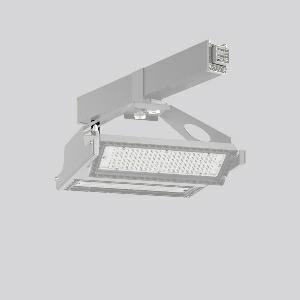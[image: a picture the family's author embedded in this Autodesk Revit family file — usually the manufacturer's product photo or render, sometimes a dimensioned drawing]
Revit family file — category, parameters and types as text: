
# Revit family: linedo_lightcase_950660_840_776_hb0_ed7c
name_source: partatom
category: Lighting Fixtures
units: mm (PartAtom-declared; Revit-internal decimal feet)

## family parameters
Cut with Voids When Loaded = No
Host = Face
Light Source = No
Part Type = Normal
Room Calculation Point = No
Round Connector Dimension = Use Diameter
Shared = No

## types (1)
- LINEDO_Lightcase (1 x LED Modul 840, 17700 lm, 4000)
    Apparent Load = 234 VA
    CIE Flux Codes = 85 97 100 100 100
    Color Rendering = 80
    Color Temperature = 4000
    Default Elevation = 1800 mm
    Description = LINEDO, 117 W, 17700 lm, 840, silver, DALI
Continuous line luminaire, L 598 B 400 H 280
    Height = 280 mm
    Lamp = 1 x LED Modul 840
    Lamp Light Flux = 17700 lm
    Lamp count = 1
    Length = 598 mm
    Lifetime = 50000 h
    Luminous efficacy = 151 lm/W
    Manufacturer = RZB
    ModVariant = No
    Model = 950660.840.776.HB0
    Mounting Place = Ceiling
    Mounting Type = Surface mounted, Pendant
    Number of Poles = 1
    OnlyDefault = Yes
    Power Factor = 1
    Product Name = LINEDO_Lightcase
    Product group = Continuous line luminaire system Linedo IP 54
    ProductGroupID = 314
    Protection Class = Protection class I
    Protection Degree = IP 54
    RLX_Detail_Level = 1
    RLX_Emergency_Light_Flux = 0 lm
    RLX_Emergency_Type = 0
    RLX_Emergency_Type_DB = No
    RlxData = <blob elided: 38493 chars, md5=87ff5631>
    Socket = socket
    Standby Power = 0 W
    System Light Flux = 35400 lm
    System Power = 234 W
    Type Comments = Product without accessories
    Type Image = 950660.840.476.hb0.jpg
    URL = http://relux.com
    VarID = ---
    Voltage = 230 V
    Voltage Range = 220-240 V
    Weight = 0.00 kg
    Width = 400 mm

## geometry (parser evidence)
native form markers: Blend x4, Sweep x15
no freeform markers — native parametric forms only
